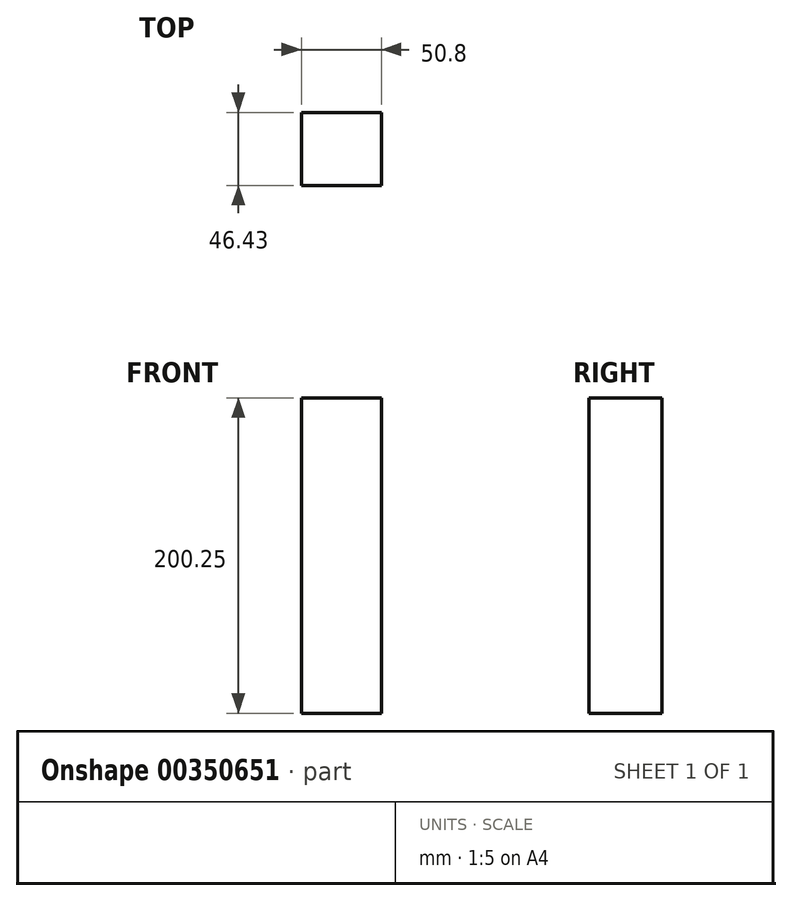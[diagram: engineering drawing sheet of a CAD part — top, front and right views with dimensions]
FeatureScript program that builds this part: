
annotation { "Feature Type Name" : "Feature", "Feature Type Description" : "" }
export const myFeature = defineFeature(function(context is Context, id is Id, definition is map)
    precondition{}
    {
        {
            var Q0;
            Q0=qCreatedBy(makeId("Right.planeOp"),FACE);
            var sketch = newSketch(context, id + "F0", { "sketchPlane" : qUnion([Q0])});
            skLineSegment(sketch, "E0.bottom", {"start": v(-46.43, 89.39) * mm, "end": v(0, 89.39) * mm});
            skLineSegment(sketch, "E0.top", {"start": v(-46.43, -110.86) * mm, "end": v(0, -110.86) * mm});
            skLineSegment(sketch, "E0.left", {"start": v(-46.43, 89.39) * mm, "end": v(-46.43, -110.86) * mm});
            skLineSegment(sketch, "E0.right", {"start": v(0, 89.39) * mm, "end": v(0, -110.86) * mm});
            skSolve(sketch);
        }
        {
            var Q0;
            Q0 = qSketchRegion(id + "F0", true);
            extrude(context, id + "F1", {"entities" : qUnion([Q0]), "depth" : 50.8 * mm});
        }
    });
